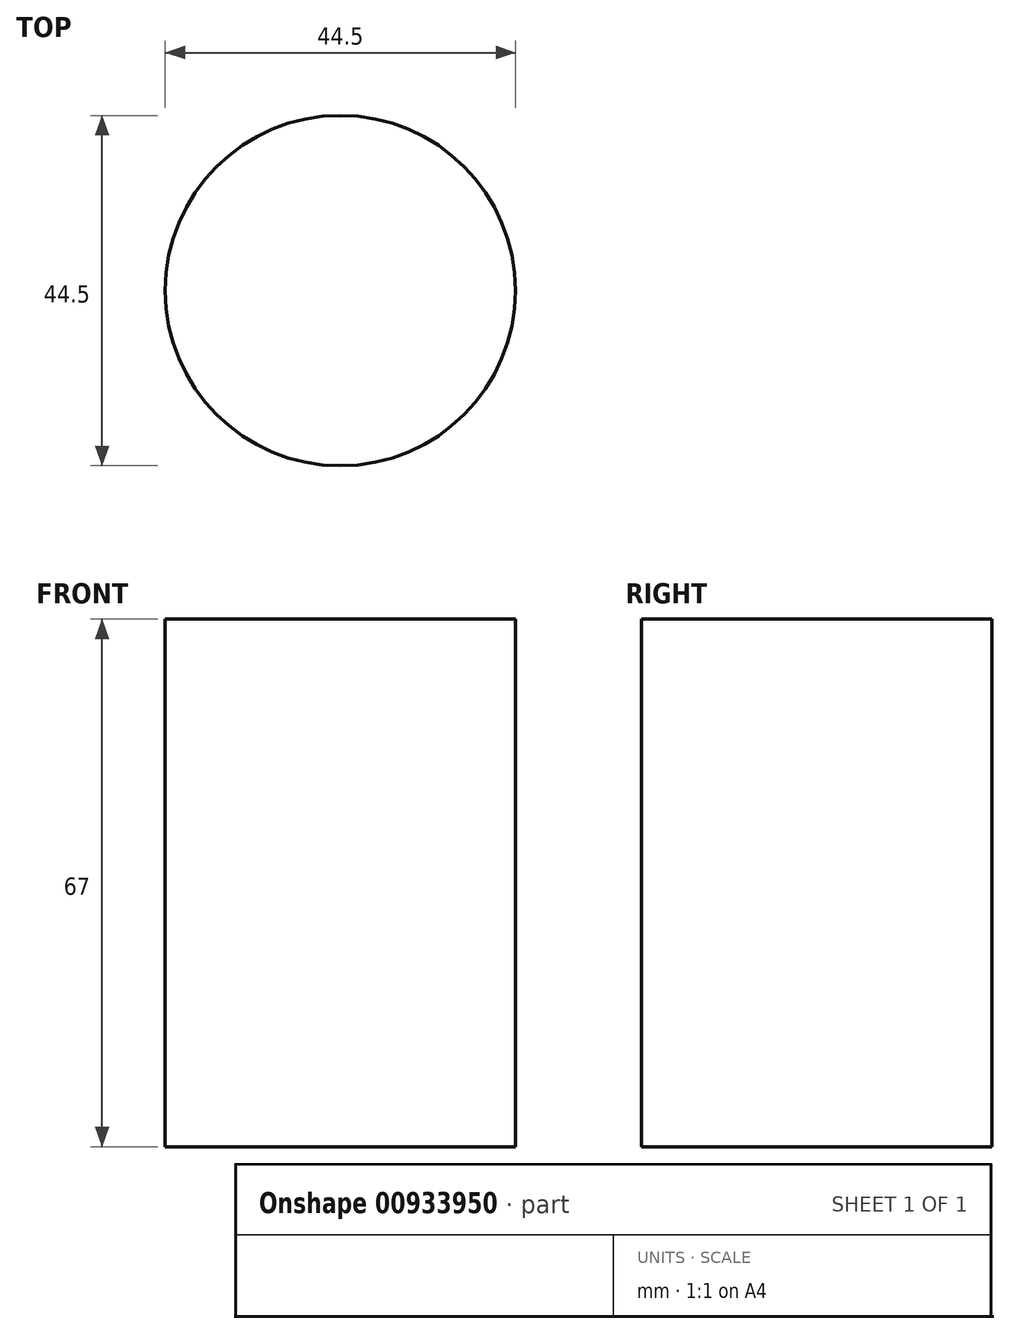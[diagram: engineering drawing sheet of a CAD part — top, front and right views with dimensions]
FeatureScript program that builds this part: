
annotation { "Feature Type Name" : "Feature", "Feature Type Description" : "" }
export const myFeature = defineFeature(function(context is Context, id is Id, definition is map)
    precondition{}
    {
        {
            var Q0;
            Q0=qCreatedBy(makeId("Top.planeOp"),FACE);
            var sketch = newSketch(context, id + "F0", { "sketchPlane" : qUnion([Q0])});
            skCircle(sketch, "E0", {"center": v(0, 0) * mm, "radius": 22.25 * mm});
            skSolve(sketch);
        }
        {
            var Q0;
            Q0=makeQuery(id+"F0.imprint","IMPRINT",FACE,{"disambiguationData":[TD([[makeQuery(id+"F0.imprint","IMPRINT",EDGE,{"derivedFrom":sQuery(id+"F0.wireOp",EDGE,"E0")}),1.0]])]});
            extrude(context, id + "F1", {"entities" : qUnion([Q0]), "depth" : 67 * mm, "offsetDistance" : 25 * mm});
        }
    });
